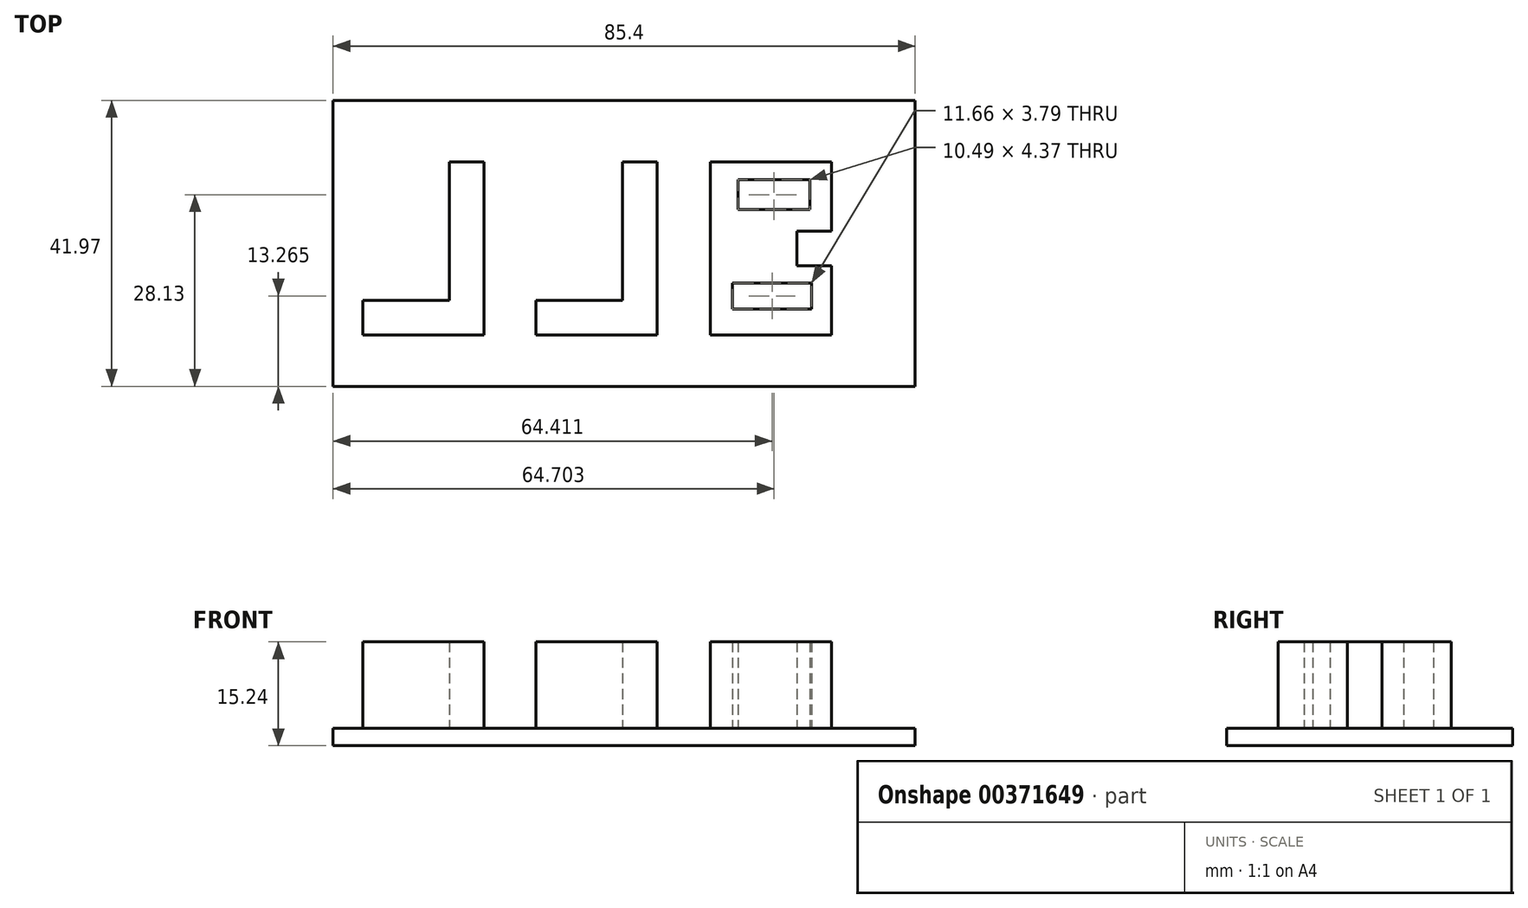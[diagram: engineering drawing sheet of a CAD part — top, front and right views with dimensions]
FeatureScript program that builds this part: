
annotation { "Feature Type Name" : "Feature", "Feature Type Description" : "" }
export const myFeature = defineFeature(function(context is Context, id is Id, definition is map)
    precondition{}
    {
        {
            var Q0;
            Q0=qCreatedBy(makeId("Top.planeOp"),FACE);
            var sketch = newSketch(context, id + "F0", { "sketchPlane" : qUnion([Q0])});
            skLineSegment(sketch, "E0", {"start": v(9.08, 0) * mm, "end": v(9.08, 12.7) * mm});
            skLineSegment(sketch, "E1", {"start": v(9.08, 12.7) * mm, "end": v(4, 12.7) * mm});
            skLineSegment(sketch, "E2", {"start": v(4, 12.7) * mm, "end": v(4, -7.62) * mm});
            skLineSegment(sketch, "E3", {"start": v(4, -7.62) * mm, "end": v(-8.7, -7.62) * mm});
            skLineSegment(sketch, "E4", {"start": v(-8.7, -7.62) * mm, "end": v(-8.7, -12.7) * mm});
            skLineSegment(sketch, "E5", {"start": v(-8.7, -12.7) * mm, "end": v(9.08, -12.7) * mm});
            skLineSegment(sketch, "E6", {"start": v(9.08, -12.7) * mm, "end": v(9.08, 0) * mm});
            skLineSegment(sketch, "E7", {"start": v(-16.32, -12.7) * mm, "end": v(-16.32, 12.7) * mm});
            skLineSegment(sketch, "E8", {"start": v(-16.32, 12.7) * mm, "end": v(-21.4, 12.7) * mm});
            skLineSegment(sketch, "E9", {"start": v(-21.4, 12.7) * mm, "end": v(-21.4, -7.62) * mm});
            skLineSegment(sketch, "E10", {"start": v(-21.4, -7.62) * mm, "end": v(-34.1, -7.62) * mm});
            skLineSegment(sketch, "E11", {"start": v(-34.1, -7.62) * mm, "end": v(-34.1, -12.7) * mm});
            skLineSegment(sketch, "E12", {"start": v(-34.1, -12.7) * mm, "end": v(-16.32, -12.7) * mm});
            skLineSegment(sketch, "E13", {"start": v(9.08, -12.7) * mm, "end": v(16.9, -12.7) * mm});
            skLineSegment(sketch, "E14", {"start": v(16.9, -12.7) * mm, "end": v(16.9, 12.7) * mm});
            skLineSegment(sketch, "E15", {"start": v(16.9, 12.7) * mm, "end": v(34.69, 12.7) * mm});
            skLineSegment(sketch, "E16", {"start": v(34.69, 12.7) * mm, "end": v(34.69, 2.54) * mm});
            skLineSegment(sketch, "E17", {"start": v(34.69, 2.54) * mm, "end": v(29.6, 2.54) * mm});
            skLineSegment(sketch, "E18", {"start": v(29.6, 2.54) * mm, "end": v(29.6, -2.54) * mm});
            skLineSegment(sketch, "E19", {"start": v(29.6, -2.54) * mm, "end": v(34.69, -2.54) * mm});
            skLineSegment(sketch, "E20", {"start": v(34.69, -2.54) * mm, "end": v(34.69, -12.7) * mm});
            skLineSegment(sketch, "E21", {"start": v(34.69, -12.7) * mm, "end": v(16.9, -12.7) * mm});
            skLineSegment(sketch, "E22.bottom", {"start": v(20.99, 5.68) * mm, "end": v(31.48, 5.68) * mm});
            skLineSegment(sketch, "E22.top", {"start": v(20.99, 10.06) * mm, "end": v(31.48, 10.06) * mm});
            skLineSegment(sketch, "E22.left", {"start": v(20.99, 5.68) * mm, "end": v(20.99, 10.06) * mm});
            skLineSegment(sketch, "E22.right", {"start": v(31.48, 5.68) * mm, "end": v(31.48, 10.06) * mm});
            skLineSegment(sketch, "E23.bottom", {"start": v(20.11, -8.9) * mm, "end": v(31.77, -8.9) * mm});
            skLineSegment(sketch, "E23.top", {"start": v(20.11, -5.1) * mm, "end": v(31.77, -5.1) * mm});
            skLineSegment(sketch, "E23.left", {"start": v(20.11, -8.9) * mm, "end": v(20.11, -5.1) * mm});
            skLineSegment(sketch, "E23.right", {"start": v(31.77, -8.9) * mm, "end": v(31.77, -5.1) * mm});
            skSolve(sketch);
        }
        {
            var Q0;
            Q0 = qSketchRegion(id + "F0", true);
            extrude(context, id + "F1", {"entities" : qUnion([Q0]), "depth" : 12.7 * mm});
        }
        {
            var Q0;
            Q0=qCreatedBy(makeId("Top.planeOp"),FACE);
            var sketch = newSketch(context, id + "F2", { "sketchPlane" : qUnion([Q0])});
            skLineSegment(sketch, "E24.bottom", {"start": v(-38.47, -20.26) * mm, "end": v(46.93, -20.26) * mm});
            skLineSegment(sketch, "E24.top", {"start": v(-38.47, 21.71) * mm, "end": v(46.93, 21.71) * mm});
            skLineSegment(sketch, "E24.left", {"start": v(-38.47, -20.26) * mm, "end": v(-38.47, 21.71) * mm});
            skLineSegment(sketch, "E24.right", {"start": v(46.93, -20.26) * mm, "end": v(46.93, 21.71) * mm});
            skSolve(sketch);
        }
        {
            var Q0;
            Q0 = qSketchRegion(id + "F2", true);
            extrude(context, id + "F3", {"entities" : qUnion([Q0]), "oppositeDirection" : true, "depth" : 2.54 * mm});
        }
    });
